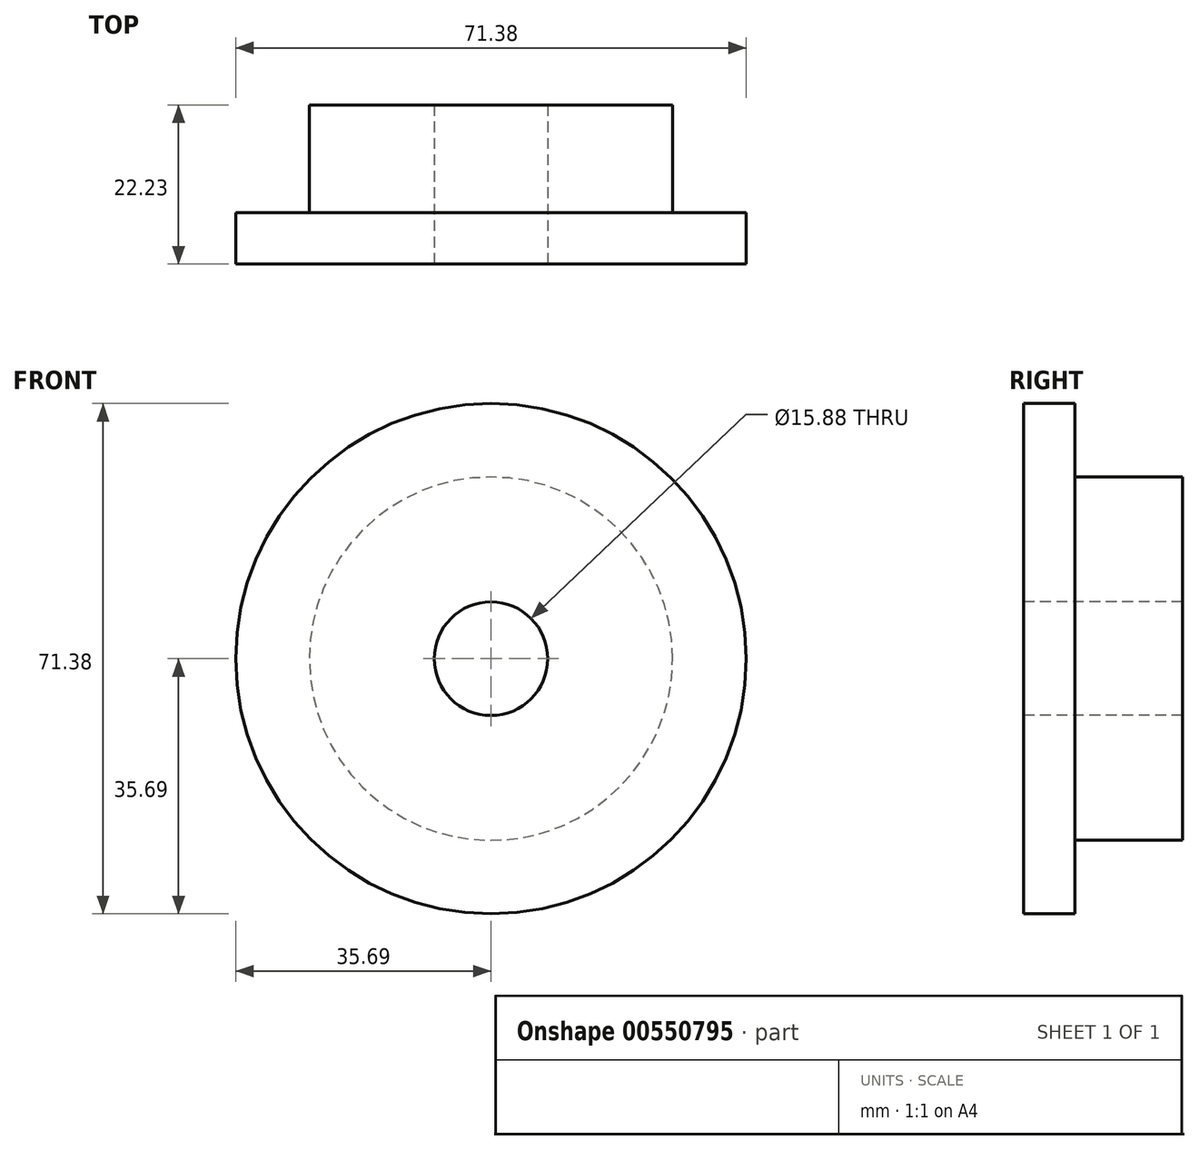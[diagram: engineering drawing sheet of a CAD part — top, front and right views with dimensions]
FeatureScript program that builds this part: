
annotation { "Feature Type Name" : "Feature", "Feature Type Description" : "" }
export const myFeature = defineFeature(function(context is Context, id is Id, definition is map)
    precondition{}
    {
        {
            var Q0;
            Q0=qCreatedBy(makeId("Right.planeOp"),FACE);
            var sketch = newSketch(context, id + "F0", { "sketchPlane" : qUnion([Q0])});
            skLineSegment(sketch, "E0", {"start": v(0, 0) * mm, "end": v(22.23, 0) * mm, "construction": true});
            skLineSegment(sketch, "E1.bottom", {"start": v(0, 7.94) * mm, "end": v(7.21, 7.94) * mm, "construction": true});
            skLineSegment(sketch, "E1.top", {"start": v(0, 35.69) * mm, "end": v(7.21, 35.69) * mm, "construction": true});
            skLineSegment(sketch, "E1.left", {"start": v(0, 7.94) * mm, "end": v(0, 35.69) * mm, "construction": true});
            skLineSegment(sketch, "E1.right", {"start": v(7.21, 7.94) * mm, "end": v(7.21, 35.69) * mm});
            skLineSegment(sketch, "E2.bottom", {"start": v(0, 7.94) * mm, "end": v(22.23, 7.94) * mm});
            skLineSegment(sketch, "E2.top", {"start": v(0, 25.4) * mm, "end": v(22.23, 25.4) * mm});
            skLineSegment(sketch, "E2.left", {"start": v(0, 7.94) * mm, "end": v(0, 25.4) * mm});
            skLineSegment(sketch, "E2.right", {"start": v(22.23, 7.94) * mm, "end": v(22.22, 25.4) * mm});
            skLineSegment(sketch, "E3.MirrorCS", {"start": v(0, -7.94) * mm, "end": v(7.21, -7.94) * mm, "construction": true});
            skLineSegment(sketch, "E4.MirrorCS", {"start": v(22.23, -7.94) * mm, "end": v(22.23, -25.4) * mm});
            skLineSegment(sketch, "E5.MirrorCS", {"start": v(0, -7.94) * mm, "end": v(0, -25.4) * mm});
            skLineSegment(sketch, "E6.MirrorCS", {"start": v(0, -7.94) * mm, "end": v(22.23, -7.94) * mm});
            skLineSegment(sketch, "E7.MirrorCS", {"start": v(0, -7.94) * mm, "end": v(0, -35.69) * mm, "construction": true});
            skLineSegment(sketch, "E8.MirrorCS", {"start": v(0, -35.69) * mm, "end": v(7.21, -35.69) * mm, "construction": true});
            skLineSegment(sketch, "E9.MirrorCS", {"start": v(7.21, -7.94) * mm, "end": v(7.21, -35.69) * mm, "construction": true});
            skLineSegment(sketch, "E10.MirrorCS", {"start": v(0, -25.4) * mm, "end": v(22.23, -25.4) * mm});
            skLineSegment(sketch, "E11.bottom", {"start": v(0, -7.94) * mm, "end": v(7.21, -7.94) * mm});
            skLineSegment(sketch, "E11.top", {"start": v(0, -35.69) * mm, "end": v(7.21, -35.69) * mm});
            skLineSegment(sketch, "E11.left", {"start": v(0, -7.94) * mm, "end": v(0, -35.69) * mm});
            skLineSegment(sketch, "E11.right", {"start": v(7.21, -7.94) * mm, "end": v(7.21, -35.69) * mm});
            skLineSegment(sketch, "E12.bottom", {"start": v(0, 35.69) * mm, "end": v(7.21, 35.69) * mm});
            skLineSegment(sketch, "E12.top", {"start": v(0, 7.94) * mm, "end": v(7.21, 7.94) * mm});
            skLineSegment(sketch, "E12.left", {"start": v(0, 35.69) * mm, "end": v(0, 7.94) * mm});
            skLineSegment(sketch, "E12.right", {"start": v(7.21, 35.69) * mm, "end": v(7.21, 7.94) * mm});
            skSolve(sketch);
        }
        {
            var Q0;
            {var subQ5=sQuery(id+"F0.wireOp",EDGE,"E12.bottom");Q0=makeQuery(id+"F0.imprint","IMPRINT",FACE,{"disambiguationData":[TD([[makeQuery(id+"F0.imprint","IMPRINT",EDGE,{"derivedFrom":subQ5}),-1.0]])]});}
            var Q1;
            {var subQ5=sQuery(id+"F0.wireOp",EDGE,"E12.top");Q1=makeQuery(id+"F0.imprint","IMPRINT",FACE,{"disambiguationData":[TD([[makeQuery(id+"F0.imprint","IMPRINT",EDGE,{"derivedFrom":subQ5}),1.0]])]});}
            var Q2;
            {var subQ0=sQuery(id+"F0.wireOp",EDGE,"E2.bottom");Q2=makeQuery(id+"F0.imprint","IMPRINT",FACE,{"disambiguationData":[TD([[makeQuery(id+"F0.imprint","IMPRINT",EDGE,{"derivedFrom":subQ0}),1.0]])]});}
            var Q3;
            Q3=sQuery(id+"F0.wireOp",EDGE,"E0");
            revolve(context, id + "F1", {"entities" : qUnion([Q0, Q1, Q2]), "axis" : qUnion([Q3]), "revolveType" : RevolveType.FULL});
        }
    });
